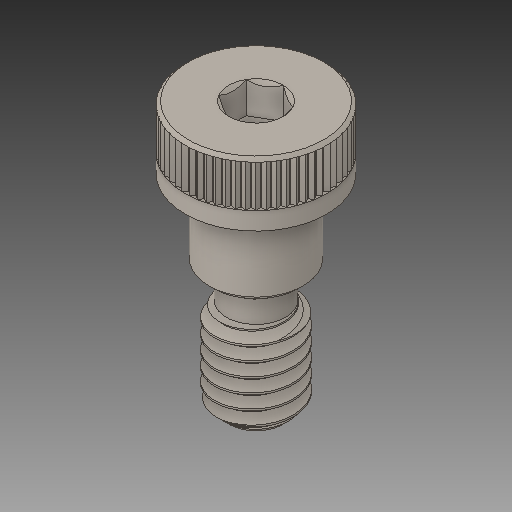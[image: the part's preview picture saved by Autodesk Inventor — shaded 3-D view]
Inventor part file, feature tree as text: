
AUTODESK INVENTOR PART (.ipt)
format: ipt  version: 2019.4 (Build 234330000, 330)  size: 606,720 bytes
history: native  units: in
note: dims shown in document units (in); Inventor stores cm internally (conversion verified against a paired STEP export)
features: chamfer x1
ambient origin geometry x8: Origin, YZ Plane, XZ Plane, XY Plane, X Axis, Y Axis, Z Axis, Center Point
bodies: Solid1 (feature_tree)
feature tree (1):
  chamfer  "Chamfer3"  [1 undecoded]
note: 1 required parameter value undecoded (feature->parameter linkage not recoverable at this tier; creation-order binding heuristic only, values carry confidence <= 0.55)
